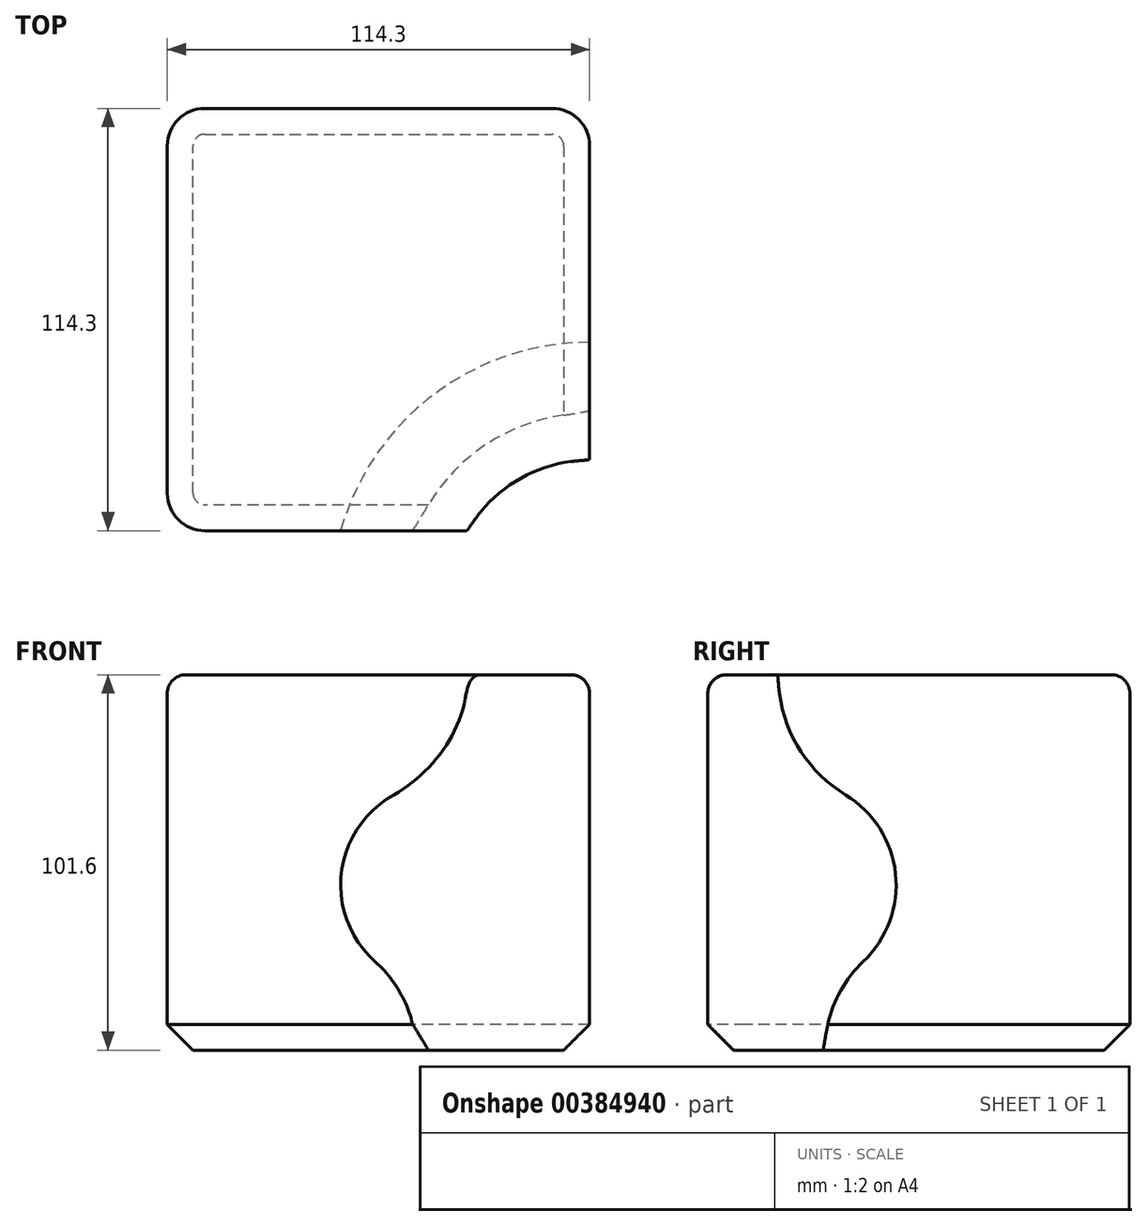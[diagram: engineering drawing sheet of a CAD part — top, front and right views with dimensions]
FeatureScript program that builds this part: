
annotation { "Feature Type Name" : "Feature", "Feature Type Description" : "" }
export const myFeature = defineFeature(function(context is Context, id is Id, definition is map)
    precondition{}
    {
        {
            var Q0;
            Q0=qCreatedBy(makeId("Top.planeOp"),FACE);
            var sketch = newSketch(context, id + "F0", { "sketchPlane" : qUnion([Q0])});
            skLineSegment(sketch, "E0.bottom", {"start": v(57.15, 57.15) * mm, "end": v(-57.15, 57.15) * mm});
            skLineSegment(sketch, "E0.top", {"start": v(57.15, -57.15) * mm, "end": v(-57.15, -57.15) * mm});
            skLineSegment(sketch, "E0.left", {"start": v(57.15, 57.15) * mm, "end": v(57.15, -57.15) * mm});
            skLineSegment(sketch, "E0.right", {"start": v(-57.15, 57.15) * mm, "end": v(-57.15, -57.15) * mm});
            skPoint(sketch, "E0.middle", {"position": v(0, 0) * mm});
            skSolve(sketch);
        }
        {
            var Q0;
            Q0 = qSketchRegion(id + "F0", true);
            extrude(context, id + "F1", {"entities" : qUnion([Q0]), "endBound" : BoundingType.SYMMETRIC, "depth" : 101.6 * mm});
        }
        {
            var Q0;
            Q0=qCreatedBy(makeId("Right.planeOp"),FACE);
            var Q1;
            Q1=makeQuery(id+"F1.opExtrude","CAP_VERTEX",VERTEX,{"disambiguationData":[OSD([sQuery(id+"F0.wireOp",EDGE,"E0.top"),sQuery(id+"F0.wireOp",EDGE,"E0.left")])],"isStart":false});
            cPlane(context, id + "F2", {"entities" : qUnion([Q0, Q1]), "cplaneType" : CPlaneType.PLANE_POINT, "offset" : 82.55 * mm, "width" : 152.4 * mm, "height" : 152.4 * mm});
        }
        {
            var Q0;
            Q0=qCreatedBy(id+"F2.planeOp",FACE);
            var sketch = newSketch(context, id + "F3", { "sketchPlane" : qUnion([Q0])});
            skLineSegment(sketch, "E1.0", {"start": v(57.15, 50.8) * mm, "end": v(-57.15, 50.8) * mm, "construction": true});
            skLineSegment(sketch, "E2", {"start": v(-76.2, 50.8) * mm, "end": v(-38.1, 50.8) * mm});
            skLineSegment(sketch, "E3", {"start": v(-38.1, 50.8) * mm, "end": v(-38.1, 105.09) * mm, "construction": true});
            skArc(sketch, "E4", {"start": v(-38.1, 50.8) * mm, "mid": v(-33.23, 32.16) * mm, "end": v(-19.86, 18.29) * mm});
            skArc(sketch, "E5", {"start": v(-19.86, 18.29) * mm, "mid": v(-6.34, -3.1) * mm, "end": v(-15.1, -26.84) * mm});
            skArc(sketch, "E6", {"start": v(-15.1, -26.84) * mm, "mid": v(-22.72, -37.76) * mm, "end": v(-25.4, -50.8) * mm});
            skLineSegment(sketch, "E7", {"start": v(-25.4, -50.8) * mm, "end": v(-76.2, -50.8) * mm});
            skLineSegment(sketch, "E8", {"start": v(-76.2, -50.8) * mm, "end": v(-76.2, 50.8) * mm});
            skLineSegment(sketch, "E9", {"start": v(-76.2, 50.8) * mm, "end": v(-76.2, 75.99) * mm, "construction": true});
            skSolve(sketch);
        }
        {
            var Q0;
            Q0 = qSketchRegion(id + "F3", true);
            var Q1;
            Q1=sQuery(id+"F3.wireOp",EDGE,"E9");
            revolve(context, id + "F4", {"operationType" : NewBodyOperationType.REMOVE, "entities" : qUnion([Q0]), "axis" : qUnion([Q1]), "revolveType" : RevolveType.FULL, "oppositeDirection" : true});
        }
        {
            var Q0;
            Q0=makeQuery(id+"F1.opExtrude","SWEPT_EDGE",EDGE,{"disambiguationData":[OSD([sQuery(id+"F0.wireOp",EDGE,"E0.bottom"),sQuery(id+"F0.wireOp",EDGE,"E0.left")])]});
            var Q1;
            Q1=makeQuery(id+"F1.opExtrude","SWEPT_EDGE",EDGE,{"disambiguationData":[OSD([sQuery(id+"F0.wireOp",EDGE,"E0.top"),sQuery(id+"F0.wireOp",EDGE,"E0.right")])]});
            var Q2;
            Q2=makeQuery(id+"F1.opExtrude","SWEPT_EDGE",EDGE,{"disambiguationData":[OSD([sQuery(id+"F0.wireOp",EDGE,"E0.bottom"),sQuery(id+"F0.wireOp",EDGE,"E0.right")])]});
            fillet(context, id + "F5", {"entities" : qUnion([Q0, Q1, Q2]), "radius" : 10.16 * mm, "tangentPropagation" : true, "allowEdgeOverflow" : false});
        }
        {
            var Q0;
            Q0=makeQuery(id+"F1.opExtrude","CAP_EDGE",EDGE,{"disambiguationData":[OSD([sQuery(id+"F0.wireOp",EDGE,"E0.top")])],"isStart":false});
            fillet(context, id + "F6", {"entities" : qUnion([Q0]), "radius" : 5.08 * mm, "tangentPropagation" : true, "allowEdgeOverflow" : false});
        }
        {
            var Q0;
            Q0=makeQuery(id+"F1.opExtrude","CAP_EDGE",EDGE,{"disambiguationData":[OSD([sQuery(id+"F0.wireOp",EDGE,"E0.top")])],"isStart":true});
            chamfer(context, id + "F7", {"entities" : qUnion([Q0]), "width" : 7 * mm, "tangentPropagation" : true});
        }
    });
